FCSTD DOCUMENT  (FreeCAD 0.19R24291 (Git))
Label: Problem03
License: All rights reserved
LicenseURL: http://en.wikipedia.org/wiki/All_rights_reserved
objects: App::FeaturePython×38, Part::Mirroring×18, Part::Part2DObjectPython×13
note: 31 computed .brp shape members not serialized (recipe doc carries the construction recipe); baked Part::Feature solids carry a one-line shape summary decoded from their .brp

FEATURE [Part::Part2DObjectPython] Line  # Draft 2D object (typed FeaturePython)
  Area = 0
  ChamferSize = 0
  Closed = false
  End = (-120,80,0)
  FilletRadius = 0
  Length = 120
  MakeFace = false
  Points = (2) [(-4.89859e-15,80,0),(-120,80,0)]
  Start = (-4.9e-15,80,0)
  Subdivisions = 0
FEATURE [Part::Part2DObjectPython] Line001  # Draft 2D object (typed FeaturePython)
  Area = 0
  ChamferSize = 0
  Closed = false
  End = (-120,-1.42e-14,0)
  FilletRadius = 0
  Length = 120
  MakeFace = false
  Points = (2) [(4.57532e-15,0,0),(-120,-1.42109e-14,0)]
  Start = (4.6e-15,0,0)
  Subdivisions = 0
FEATURE [Part::Part2DObjectPython] Line002  # Draft 2D object (typed FeaturePython)
  Area = 0
  ChamferSize = 0
  Closed = false
  End = (-120,-1.42e-14,0)
  FilletRadius = 0
  Length = 80
  MakeFace = false
  Placement = pos=(-120,80,0) rot=(0,0,1;0rad)
  Points = (2) [(0,0,0),(1.42109e-14,-80,0)]
  Start = (-120,80,0)
  Subdivisions = 7
FEATURE [Part::Part2DObjectPython] Line003  # Draft 2D object (typed FeaturePython)
  Area = 0
  ChamferSize = 0
  Closed = false
  End = (4.6e-15,0,0)
  FilletRadius = 0
  Length = 80
  MakeFace = false
  Placement = pos=(-4.9e-15,80,0) rot=(0,0,1;0rad)
  Points = (2) [(0,0,0),(7.02461e-15,-80,0)]
  Start = (-4.9e-15,80,0)
  Subdivisions = 7
FEATURE [Part::Part2DObjectPython] Line004  # Draft 2D object (typed FeaturePython)
  Area = 0
  ChamferSize = 0
  Closed = false
  End = (-60,0,0)
  FilletRadius = 0
  Length = 80
  MakeFace = false
  Placement = pos=(-60,80,0) rot=(0,0,1;0rad)
  Points = (2) [(0,0,0),(2.13163e-14,-80,0)]
  Start = (-60,80,0)
  Subdivisions = 0
FEATURE [Part::Part2DObjectPython] Line005  # Draft 2D object (typed FeaturePython)
  Area = 0
  ChamferSize = 0
  Closed = false
  End = (0,40,0)
  FilletRadius = 0
  Length = 120
  MakeFace = false
  Placement = pos=(-120,40,0) rot=(0,0,1;0rad)
  Points = (2) [(0,0,0),(120,7.10543e-15,0)]
  Start = (-120,40,0)
  Subdivisions = 7
FEATURE [Part::Part2DObjectPython] Line006  # Draft 2D object (typed FeaturePython)
  Area = 0
  ChamferSize = 0
  Closed = false
  End = (-120,70,0)
  FilletRadius = 0
  Length = 60.8276
  MakeFace = false
  Placement = pos=(-60,80,0) rot=(0,0,1;0rad)
  Points = (2) [(0,0,0),(-60,-10,0)]
  Start = (-60,80,0)
  Subdivisions = 0
FEATURE [Part::Part2DObjectPython] Line007  # Draft 2D object (typed FeaturePython)
  Area = 0
  ChamferSize = 0
  Closed = false
  End = (-120,50,0)
  FilletRadius = 0
  Length = 67.082
  MakeFace = false
  Placement = pos=(-60,80,0) rot=(0,0,1;0rad)
  Points = (2) [(0,0,0),(-60,-30,0)]
  Start = (-60,80,0)
  Subdivisions = 0
FEATURE [Part::Part2DObjectPython] Line008  # Draft 2D object (typed FeaturePython)
  Area = 0
  ChamferSize = 0
  Closed = false
  End = (-120,60,0)
  FilletRadius = 0
  Length = 63.2456
  MakeFace = false
  Placement = pos=(-60,80,0) rot=(0,0,1;0rad)
  Points = (2) [(0,0,0),(-60,-20,0)]
  Start = (-60,80,0)
  Subdivisions = 0
FEATURE [Part::Mirroring] mirror  label="Line007 (mirrored)"
  Base = (-105,40,0)
  Normal = (2e-16,-1,0)
  Source = -> Line007
FEATURE [Part::Mirroring] mirror001  label="Line008 (mirrored)"
  Base = (-105,40,0)
  Normal = (2e-16,-1,0)
  Source = -> Line008
FEATURE [Part::Mirroring] mirror002  label="Line006 (mirrored)"
  Base = (-105,40,0)
  Normal = (2e-16,-1,0)
  Source = -> Line006
FEATURE [Part::Mirroring] mirror003  label="Line008 (mirrored) (mirrored)"
  Base = (-60,0,0)
  Normal = (1,3e-16,0)
  Source = -> mirror001
FEATURE [Part::Mirroring] mirror004  label="Line007 (mirrored) (mirrored)"
  Base = (-60,0,0)
  Normal = (1,3e-16,0)
  Source = -> mirror
FEATURE [Part::Mirroring] mirror005  label="Line006 (mirrored) (mirrored)"
  Base = (-60,0,0)
  Normal = (1,3e-16,0)
  Source = -> mirror002
FEATURE [Part::Mirroring] mirror006  label="Line007 (mirrored) (mirrored) (mirrored)"
  Base = (-60,40,0)
  Normal = (1e-16,-1,0)
  Source = -> mirror004
FEATURE [Part::Mirroring] mirror007  label="Line008 (mirrored) (mirrored) (mirrored)"
  Base = (-60,40,0)
  Normal = (1e-16,-1,0)
  Source = -> mirror003
FEATURE [Part::Mirroring] mirror008  label="Line006 (mirrored) (mirrored) (mirrored)"
  Base = (-60,40,0)
  Normal = (1e-16,-1,0)
  Source = -> mirror005
FEATURE [Part::Part2DObjectPython] Line009  # Draft 2D object (typed FeaturePython)
  Area = 0
  ChamferSize = 0
  Closed = false
  End = (-60,80,0)
  FilletRadius = 0
  Length = 77.0662
  MakeFace = false
  Placement = pos=(-60,80,0) rot=(0,0,1;0rad)
  Points = (2) [(-57.6,-51.2,0),(0,0,0)]
  Start = (-117.6,28.8,0)
  Subdivisions = 0
FEATURE [Part::Part2DObjectPython] Line010  # Draft 2D object (typed FeaturePython)
  Area = 0
  ChamferSize = 0
  Closed = false
  End = (-60,80,0)
  FilletRadius = 0
  Length = 80
  MakeFace = false
  Placement = pos=(-60,80,0) rot=(0,0,1;0rad)
  Points = (2) [(-48,-64,0),(-7.10543e-15,0,0)]
  Start = (-108,16,0)
  Subdivisions = 0
FEATURE [Part::Part2DObjectPython] Line011  # Draft 2D object (typed FeaturePython)
  Area = 0
  ChamferSize = 0
  Closed = false
  End = (-60,80,0)
  FilletRadius = 0
  Length = 80.4142
  MakeFace = false
  Placement = pos=(-60,80,0) rot=(0,0,1;0rad)
  Points = (2) [(-28.2353,-75.2941,0),(0,0,0)]
  Start = (-88.2353,4.70588,0)
  Subdivisions = 0
FEATURE [Part::Mirroring] mirror009  label="Line009 (mirrored)"
  Base = (-120,40,0)
  Normal = (1e-16,-1,0)
  Source = -> Line009
FEATURE [Part::Mirroring] mirror010  label="Line010 (mirrored)"
  Base = (-120,40,0)
  Normal = (1e-16,-1,0)
  Source = -> Line010
FEATURE [Part::Mirroring] mirror011  label="Line011 (mirrored)"
  Base = (-120,40,0)
  Normal = (1e-16,-1,0)
  Source = -> Line011
FEATURE [Part::Mirroring] mirror012  label="Line009 (mirrored)001"
  Base = (-60,80,0)
  Normal = (-1,-3e-16,0)
  Source = -> Line009
FEATURE [Part::Mirroring] mirror013  label="Line011 (mirrored) (mirrored)"
  Base = (-60,80,0)
  Normal = (-1,-3e-16,0)
  Source = -> mirror011
FEATURE [Part::Mirroring] mirror014  label="Line010 (mirrored) (mirrored)"
  Base = (-60,80,0)
  Normal = (-1,-3e-16,0)
  Source = -> mirror010
FEATURE [Part::Mirroring] mirror015  label="Line009 (mirrored) (mirrored)"
  Base = (-60,80,0)
  Normal = (-1,-3e-16,0)
  Source = -> mirror009
FEATURE [Part::Mirroring] mirror016  label="Line010 (mirrored)001"
  Base = (-60,80,0)
  Normal = (-1,-3e-16,0)
  Source = -> Line010
FEATURE [Part::Mirroring] mirror017  label="Line011 (mirrored)001"
  Base = (-60,80,0)
  Normal = (-1,-3e-16,0)
  Source = -> Line011
FEATURE [Part::Part2DObjectPython] BSpline  # Draft 2D object (typed FeaturePython)
  Area = 0
  Closed = true
  MakeFace = false
  Parameterization = 1
  Points = (16) [(-60,80,0),(-88.2353,75.2941,0),(-108,64,0),(-117.6,51.2,0),(-120,40,0),(-117.6,28.8,0),(-108,16,0),(-88.2353,4.70588,0),(-60,0,0),+7 more]
FEATURE [App::FeaturePython] Dimension  # Draft dimension (typed FeaturePython)
  Diameter = false
  Dimline = (-4.33437,94.0404,0)
  Direction = (0,0,0)
  Distance = 120
  End = (-4.9e-15,80,0)
  Normal = (0,0,1)
  Start = (-120,80,0)
FEATURE [App::FeaturePython] Dimension001  # Draft dimension (typed FeaturePython)
  Diameter = false
  Dimline = (15.1191,2.45603,0)
  Direction = (0,0,0)
  Distance = 80
  End = (4.6e-15,0,0)
  Normal = (0,0,1)
  Start = (-4.9e-15,80,0)
FEATURE [App::FeaturePython] Text  # WARN: FeaturePython — macro-defined, semantics opaque (R4)
  Placement = pos=(-125.208,37.8657,0) rot=(0,0,1;0rad)
  Text = A
FEATURE [App::FeaturePython] Text001  # WARN: FeaturePython — macro-defined, semantics opaque (R4)
  Placement = pos=(-124.771,48.1389,0) rot=(0,0,1;0rad)
  Text = 1
FEATURE [App::FeaturePython] Text002  # WARN: FeaturePython — macro-defined, semantics opaque (R4)
  Placement = pos=(-124.99,58.6307,0) rot=(0,0,1;0rad)
  Text = 2
FEATURE [App::FeaturePython] Text003  # WARN: FeaturePython — macro-defined, semantics opaque (R4)
  Placement = pos=(-125.208,68.6853,0) rot=(0,0,1;0rad)
  Text = 3
FEATURE [App::FeaturePython] Text004  # WARN: FeaturePython — macro-defined, semantics opaque (R4)
  Placement = pos=(-114.279,48.7946,0) rot=(0,0,1;0rad)
  Text = P1
FEATURE [App::FeaturePython] Text006  # WARN: FeaturePython — macro-defined, semantics opaque (R4)
  Placement = pos=(-104.443,61.035,0) rot=(0,0,1;0rad)
  Text = P2
FEATURE [App::FeaturePython] Text007  # WARN: FeaturePython — macro-defined, semantics opaque (R4)
  Placement = pos=(-85.8641,71.7454,0) rot=(0,0,1;0rad)
  Text = P3
FEATURE [App::FeaturePython] Text008  # WARN: FeaturePython — macro-defined, semantics opaque (R4)
  Placement = pos=(-31.4381,69.9968,0) rot=(0,0,1;0rad)
  Text = P5
FEATURE [App::FeaturePython] Text009  # WARN: FeaturePython — macro-defined, semantics opaque (R4)
  Placement = pos=(-13.7332,57.5378,0) rot=(0,0,1;0rad)
  Text = P6
FEATURE [App::FeaturePython] Text010  # WARN: FeaturePython — macro-defined, semantics opaque (R4)
  Placement = pos=(-6.08298,45.9531,0) rot=(0,0,1;0rad)
  Text = P7
FEATURE [App::FeaturePython] Text011  # WARN: FeaturePython — macro-defined, semantics opaque (R4)
  Placement = pos=(-125.256,80.7571,0) rot=(0,0,1;0rad)
  Text = Q
FEATURE [App::FeaturePython] Text012  # WARN: FeaturePython — macro-defined, semantics opaque (R4)
  Placement = pos=(-61.4495,82.6259,0) rot=(0,0,1;0rad)
  Text = C
FEATURE [App::FeaturePython] Text013  # WARN: FeaturePython — macro-defined, semantics opaque (R4)
  Placement = pos=(1.28897,81.0241,0) rot=(0,0,1;0rad)
  Text = R
FEATURE [App::FeaturePython] Text014  # WARN: FeaturePython — macro-defined, semantics opaque (R4)
  Placement = pos=(2.06622,39.7123,0) rot=(0,0,1;0rad)
  Text = B
FEATURE [App::FeaturePython] Text015  # WARN: FeaturePython — macro-defined, semantics opaque (R4)
  Placement = pos=(2.06622,-2.6782,0) rot=(0,0,1;0rad)
  Text = S
FEATURE [App::FeaturePython] Text016  # WARN: FeaturePython — macro-defined, semantics opaque (R4)
  Placement = pos=(-61.1934,-5.28685,0) rot=(0,0,1;0rad)
  Text = D
FEATURE [App::FeaturePython] Text017  # WARN: FeaturePython — macro-defined, semantics opaque (R4)
  Placement = pos=(-124.453,-3.98252,0) rot=(0,0,1;0rad)
  Text = P
FEATURE [App::FeaturePython] Text018  # WARN: FeaturePython — macro-defined, semantics opaque (R4)
  Placement = pos=(-57.2805,41.3427,0) rot=(0,0,1;0rad)
  Text = O
FEATURE [App::FeaturePython] Text019  # WARN: FeaturePython — macro-defined, semantics opaque (R4)
  Placement = pos=(-85.8754,-14.01,0) rot=(0,0,1;0rad)
  Text = All Dimensions are in 'mm'
FEATURE [App::FeaturePython] Text020  # WARN: FeaturePython — macro-defined, semantics opaque (R4)
  Placement = pos=(-125.337,28.1418,0) rot=(0,0,1;0rad)
  Text = 1'
FEATURE [App::FeaturePython] Text021  # WARN: FeaturePython — macro-defined, semantics opaque (R4)
  Placement = pos=(-125.337,17.828,0) rot=(0,0,1;0rad)
  Text = 2'
FEATURE [App::FeaturePython] Text022  # WARN: FeaturePython — macro-defined, semantics opaque (R4)
  Placement = pos=(-124.888,7.73853,0) rot=(0,0,1;0rad)
  Text = 3'
FEATURE [App::FeaturePython] Text023  # WARN: FeaturePython — macro-defined, semantics opaque (R4)
  Placement = pos=(-107.4,34.4197,0) rot=(0,0,1;0rad)
  Text = 6
FEATURE [App::FeaturePython] Text024  # WARN: FeaturePython — macro-defined, semantics opaque (R4)
  Placement = pos=(-90.8081,34.6439,0) rot=(0,0,1;0rad)
  Text = 5
FEATURE [App::FeaturePython] Text025  # WARN: FeaturePython — macro-defined, semantics opaque (R4)
  Placement = pos=(-60,-1.42e-14,0) rot=(0,0,1;0rad)
  Text = 4
FEATURE [App::FeaturePython] Text026  # WARN: FeaturePython — macro-defined, semantics opaque (R4)
  Placement = pos=(-71.9743,35.765,0) rot=(0,0,1;0rad)
  Text = 4
FEATURE [App::FeaturePython] Text027  # WARN: FeaturePython — macro-defined, semantics opaque (R4)
  Placement = pos=(-49.7774,36.2134,0) rot=(0,0,1;0rad)
  Text = 4'
FEATURE [App::FeaturePython] Text028  # WARN: FeaturePython — macro-defined, semantics opaque (R4)
  Placement = pos=(-36.3247,35.5407,0) rot=(0,0,1;0rad)
  Text = 5'
FEATURE [App::FeaturePython] Text029  # WARN: FeaturePython — macro-defined, semantics opaque (R4)
  Placement = pos=(-16.8183,34.4197,0) rot=(0,0,1;0rad)
  Text = 6'
FEATURE [App::FeaturePython] Text030  # WARN: FeaturePython — macro-defined, semantics opaque (R4)
  Placement = pos=(-3.81403,35.0923,0) rot=(0,0,1;0rad)
  Text = 7'
FEATURE [App::FeaturePython] Text031  # WARN: FeaturePython — macro-defined, semantics opaque (R4)
  Placement = pos=(-114.664,27.0207,0) rot=(0,0,1;0rad)
  Text = P1'
FEATURE [App::FeaturePython] Text032  # WARN: FeaturePython — macro-defined, semantics opaque (R4)
  Placement = pos=(-105.472,15.5859,0) rot=(0,0,1;0rad)
  Text = P2'
FEATURE [App::FeaturePython] Text033  # WARN: FeaturePython — macro-defined, semantics opaque (R4)
  Placement = pos=(-85.7409,4.59956,0) rot=(0,0,1;0rad)
  Text = P3'
FEATURE [App::FeaturePython] Text034  # WARN: FeaturePython — macro-defined, semantics opaque (R4)
  Placement = pos=(-31.706,1.01218,0) rot=(0,0,1;0rad)
  Text = P5'
FEATURE [App::FeaturePython] Text035  # WARN: FeaturePython — macro-defined, semantics opaque (R4)
  Placement = pos=(-11.5269,11.1017,0) rot=(0,0,1;0rad)
  Text = P6'
FEATURE [App::FeaturePython] Text036  # WARN: FeaturePython — macro-defined, semantics opaque (R4)
  Placement = pos=(-12.4238,26.3481,0) rot=(0,0,1;0rad)
  Text = P7'
